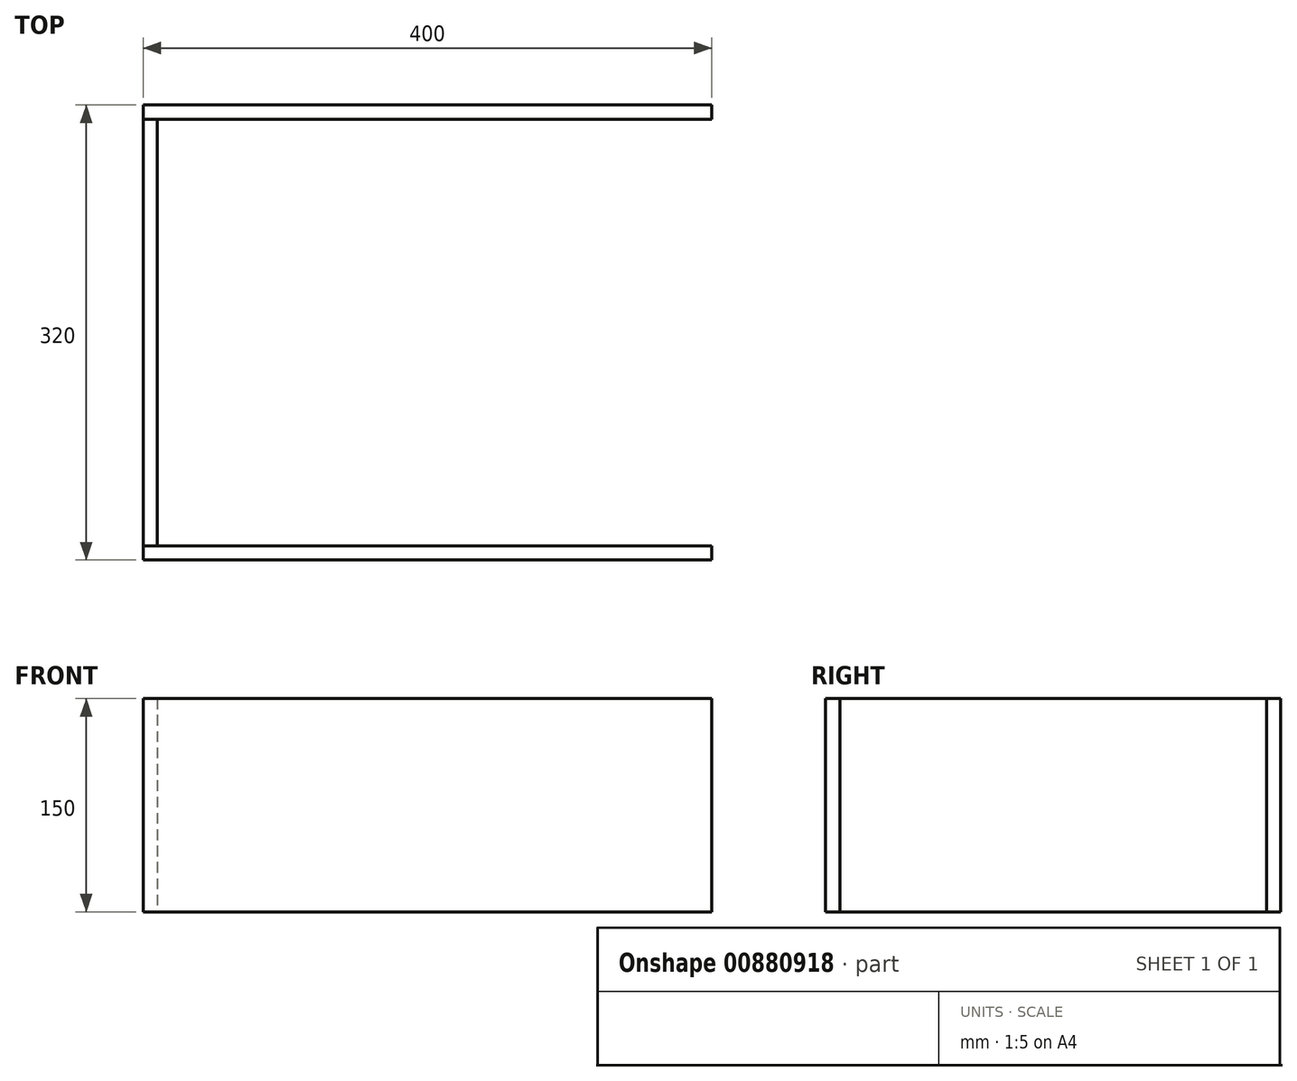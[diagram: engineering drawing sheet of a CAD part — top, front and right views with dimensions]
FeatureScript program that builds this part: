
annotation { "Feature Type Name" : "Feature", "Feature Type Description" : "" }
export const myFeature = defineFeature(function(context is Context, id is Id, definition is map)
    precondition{}
    {
        {
            var Q0;
            Q0=qCreatedBy(makeId("Right.planeOp"),FACE);
            var sketch = newSketch(context, id + "F0", { "sketchPlane" : qUnion([Q0])});
            skLineSegment(sketch, "E0.bottom", {"start": v(-150, 75) * mm, "end": v(150, 75) * mm});
            skLineSegment(sketch, "E0.top", {"start": v(-150, -75) * mm, "end": v(150, -75) * mm});
            skLineSegment(sketch, "E0.left", {"start": v(-150, 75) * mm, "end": v(-150, -75) * mm});
            skLineSegment(sketch, "E0.right", {"start": v(150, 75) * mm, "end": v(150, -75) * mm});
            skPoint(sketch, "E0.middle", {"position": v(0, 0) * mm});
            skSolve(sketch);
        }
        {
            var Q0;
            Q0=makeQuery(id+"F0.imprint","IMPRINT",FACE,{"disambiguationData":[TD([[makeQuery(id+"F0.imprint","IMPRINT",EDGE,{"derivedFrom":sQuery(id+"F0.wireOp",EDGE,"E0.bottom")}),-1.0]])]});
            extrude(context, id + "F1", {"entities" : qUnion([Q0]), "depth" : 10 * mm, "offsetDistance" : 25 * mm});
        }
        {
            var Q0;
            Q0=makeQuery(id+"F1.opExtrude","SWEPT_FACE",FACE,{"disambiguationData":[OSD([sQuery(id+"F0.wireOp",EDGE,"E0.left")])]});
            var sketch = newSketch(context, id + "F2", { "sketchPlane" : qUnion([Q0])});
            skLineSegment(sketch, "E1.bottom", {"start": v(0, -75) * mm, "end": v(400, -75) * mm});
            skLineSegment(sketch, "E1.top", {"start": v(0, 75) * mm, "end": v(400, 75) * mm});
            skLineSegment(sketch, "E1.left", {"start": v(0, -75) * mm, "end": v(0, 75) * mm});
            skLineSegment(sketch, "E1.right", {"start": v(400, -75) * mm, "end": v(400, 75) * mm});
            skSolve(sketch);
        }
        {
            var Q0;
            {var subQ2=sQuery(id+"F2.wireOp",EDGE,"E1.right");Q0=makeQuery(id+"F2.imprint","IMPRINT",FACE,{"disambiguationData":[TD([[makeQuery(id+"F2.imprint","IMPRINT",EDGE,{"derivedFrom":subQ2}),1.0]])]});}
            var Q1;
            {var subQ0=sQuery(id+"F2.wireOp",EDGE,"E1.left");Q1=makeQuery(id+"F2.imprint","IMPRINT",FACE,{"disambiguationData":[TD([[makeQuery(id+"F2.imprint","IMPRINT",EDGE,{"derivedFrom":subQ0}),1.0]])]});}
            extrude(context, id + "F3", {"entities" : qUnion([Q0, Q1]), "depth" : 10 * mm, "offsetDistance" : 25 * mm});
        }
        {
            var Q0;
            Q0=makeQuery(id+"F3.opExtrude","SWEPT_BODY",BODY,{"disambiguationData":[OSD([sQuery(id+"F0.wireOp",EDGE,"E0.left"),sQuery(id+"F2.wireOp",EDGE,"E1.bottom"),sQuery(id+"F2.wireOp",EDGE,"E1.top"),sQuery(id+"F2.wireOp",EDGE,"E1.right")])]});
            var Q1;
            Q1=qCreatedBy(makeId("Front.planeOp"),FACE);
            mirror(context, id + "F4", {"entities" : qUnion([Q0]), "mirrorPlane" : qUnion([Q1])});
        }
    });
